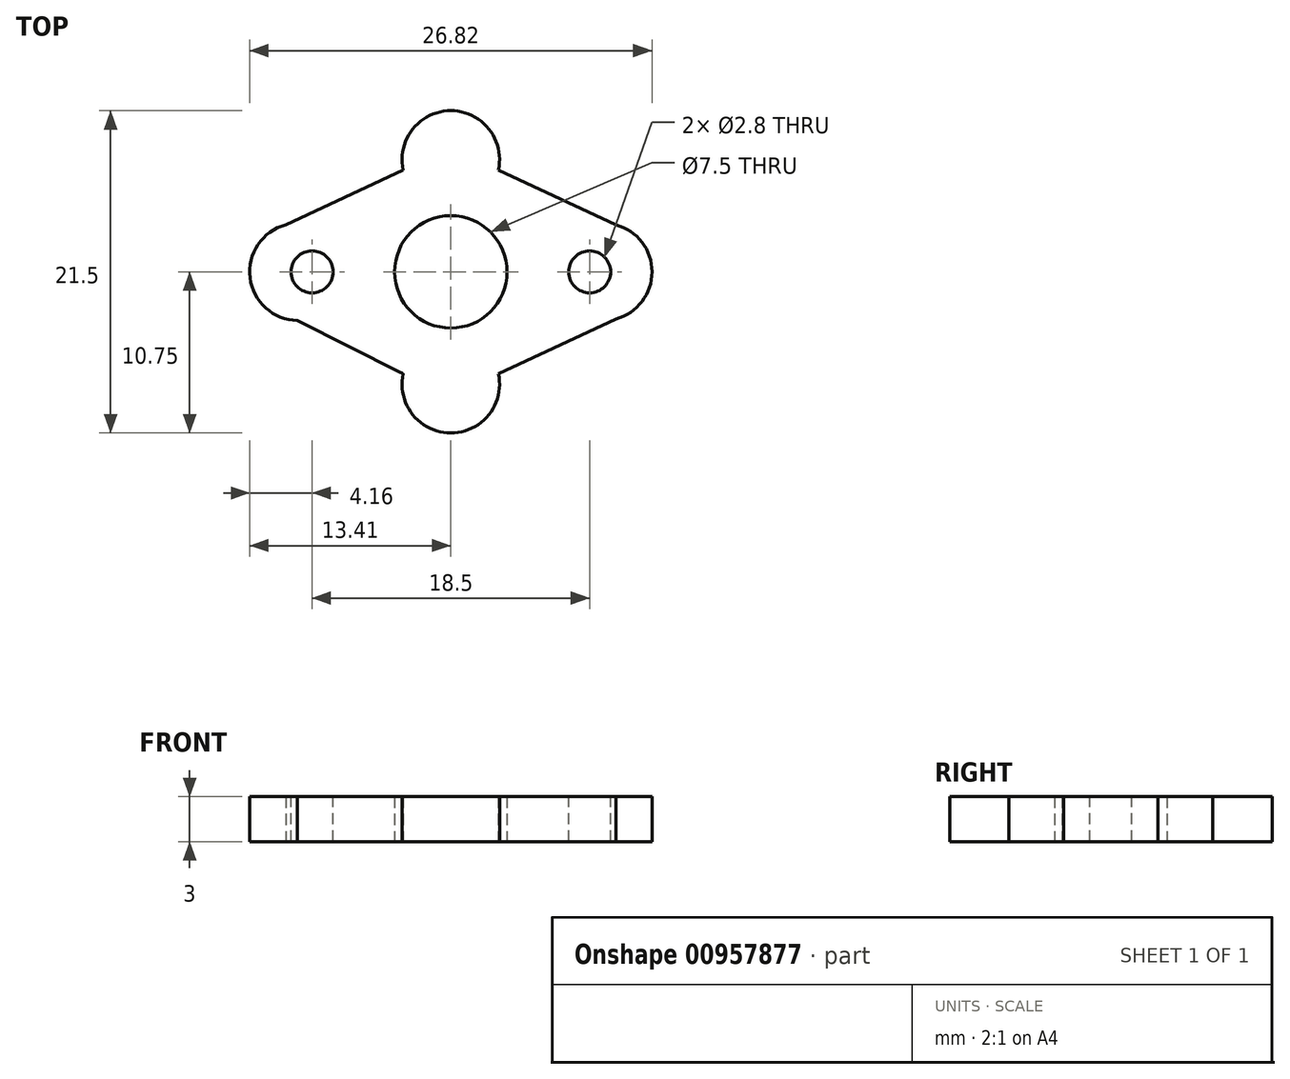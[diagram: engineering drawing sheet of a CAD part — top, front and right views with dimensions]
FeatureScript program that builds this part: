
annotation { "Feature Type Name" : "Feature", "Feature Type Description" : "" }
export const myFeature = defineFeature(function(context is Context, id is Id, definition is map)
    precondition{}
    {
        {
            var Q0;
            Q0=qCreatedBy(makeId("Top.planeOp"),FACE);
            var sketch = newSketch(context, id + "F0", { "sketchPlane" : qUnion([Q0])});
            skCircle(sketch, "E0", {"center": v(0, 0) * mm, "radius": 3.75 * mm});
            skCircle(sketch, "E1", {"center": v(0, 0) * mm, "radius": 7.5 * mm});
            skCircle(sketch, "E2", {"center": v(0, -7.5) * mm, "radius": 3.25 * mm});
            skCircle(sketch, "E3", {"center": v(10.16, 0) * mm, "radius": 3.25 * mm});
            skCircle(sketch, "E4", {"center": v(0, 7.5) * mm, "radius": 3.25 * mm});
            skCircle(sketch, "E5", {"center": v(-10.16, 0) * mm, "radius": 3.25 * mm});
            skLineSegment(sketch, "E6", {"start": v(-10.22, -3.25) * mm, "end": v(-3.17, -6.8) * mm});
            skLineSegment(sketch, "E7", {"start": v(3.17, -6.8) * mm, "end": v(11, -3.14) * mm});
            skLineSegment(sketch, "E8", {"start": v(3.17, 6.8) * mm, "end": v(11, 3.14) * mm});
            skLineSegment(sketch, "E9", {"start": v(-3.17, 6.8) * mm, "end": v(-11, 3.14) * mm});
            skSolve(sketch);
        }
        {
            var Q0;
            {var subQ0=sQuery(id+"F0.wireOp",EDGE,"E4");var subQ1=sQuery(id+"F0.wireOp",EDGE,"E1");var subQ2=makeQuery(id+"F0.imprint","INTERSECT",VERTEX,{"derivedFrom":[subQ1,subQ0,sQuery(id+"F0.wireOp",EDGE,"MsoxRcEN-taFl-h5Oa-m4Po-DjfKg65qIXiD")]});Q0=makeQuery(id+"F0.imprint","IMPRINT",FACE,{"disambiguationData":[TD([[makeQuery(id+"F0.imprint","IMPRINT",EDGE,{"disambiguationData":[TD([[subQ2,-1.0]])],"derivedFrom":subQ1}),-1.0]])]});}
            var Q1;
            {var subQ0=sQuery(id+"F0.wireOp",EDGE,"E5");var subQ1=sQuery(id+"F0.wireOp",EDGE,"E1");var subQ2=makeQuery(id+"F0.imprint","INTERSECT",VERTEX,{"derivedFrom":[subQ1,subQ0,sQuery(id+"F0.wireOp",EDGE,"5fAFj8NA-k12Z-kT6c-h5jL-KaeJKLKDLutY")]});Q1=makeQuery(id+"F0.imprint","IMPRINT",FACE,{"disambiguationData":[TD([[makeQuery(id+"F0.imprint","IMPRINT",EDGE,{"disambiguationData":[TD([[subQ2,1.0]])],"derivedFrom":subQ1}),-1.0]])]});}
            var Q2;
            {var subQ0=sQuery(id+"F0.wireOp",EDGE,"E2");var subQ1=sQuery(id+"F0.wireOp",EDGE,"E1");var subQ2=makeQuery(id+"F0.imprint","INTERSECT",VERTEX,{"derivedFrom":[subQ1,subQ0,sQuery(id+"F0.wireOp",EDGE,"5fAFj8NA-k12Z-kT6c-h5jL-KaeJKLKDLutY")]});Q2=makeQuery(id+"F0.imprint","IMPRINT",FACE,{"disambiguationData":[TD([[makeQuery(id+"F0.imprint","IMPRINT",EDGE,{"disambiguationData":[TD([[subQ2,-1.0]])],"derivedFrom":subQ1}),-1.0]])]});}
            var Q3;
            {var subQ0=sQuery(id+"F0.wireOp",EDGE,"E3");var subQ1=sQuery(id+"F0.wireOp",EDGE,"E1");var subQ2=makeQuery(id+"F0.imprint","INTERSECT",VERTEX,{"derivedFrom":[subQ1,subQ0,sQuery(id+"F0.wireOp",EDGE,"UtXMOaHf-onAp-QZEp-fR57-lMSn8MbB5BsG")]});Q3=makeQuery(id+"F0.imprint","IMPRINT",FACE,{"disambiguationData":[TD([[makeQuery(id+"F0.imprint","IMPRINT",EDGE,{"disambiguationData":[TD([[subQ2,-1.0]])],"derivedFrom":subQ1}),-1.0]])]});}
            var Q4;
            {var subQ0=sQuery(id+"F0.wireOp",EDGE,"UtXMOaHf-onAp-QZEp-fR57-lMSn8MbB5BsG");var subQ1=sQuery(id+"F0.wireOp",EDGE,"E2");var subQ3=makeQuery(id+"F0.imprint","INTERSECT",VERTEX,{"derivedFrom":[subQ1,subQ0]});Q4=makeQuery(id+"F0.imprint","IMPRINT",FACE,{"disambiguationData":[TD([[makeQuery(id+"F0.imprint","IMPRINT",EDGE,{"disambiguationData":[TD([[subQ3,1.0]])],"derivedFrom":subQ1}),1.0]])]});}
            var Q5;
            {var subQ0=sQuery(id+"F0.wireOp",EDGE,"5fAFj8NA-k12Z-kT6c-h5jL-KaeJKLKDLutY");var subQ1=sQuery(id+"F0.wireOp",EDGE,"E2");var subQ3=makeQuery(id+"F0.imprint","INTERSECT",VERTEX,{"derivedFrom":[subQ1,subQ0]});Q5=makeQuery(id+"F0.imprint","IMPRINT",FACE,{"disambiguationData":[TD([[makeQuery(id+"F0.imprint","IMPRINT",EDGE,{"disambiguationData":[TD([[subQ3,-1.0]])],"derivedFrom":subQ1}),1.0]])]});}
            var Q6;
            {var subQ0=sQuery(id+"F0.wireOp",EDGE,"MsoxRcEN-taFl-h5Oa-m4Po-DjfKg65qIXiD");var subQ1=sQuery(id+"F0.wireOp",EDGE,"E3");var subQ3=makeQuery(id+"F0.imprint","INTERSECT",VERTEX,{"derivedFrom":[subQ1,subQ0]});Q6=makeQuery(id+"F0.imprint","IMPRINT",FACE,{"disambiguationData":[TD([[makeQuery(id+"F0.imprint","IMPRINT",EDGE,{"disambiguationData":[TD([[subQ3,1.0]])],"derivedFrom":subQ1}),1.0]])]});}
            var Q7;
            {var subQ0=sQuery(id+"F0.wireOp",EDGE,"UtXMOaHf-onAp-QZEp-fR57-lMSn8MbB5BsG");var subQ1=sQuery(id+"F0.wireOp",EDGE,"E3");var subQ3=makeQuery(id+"F0.imprint","INTERSECT",VERTEX,{"derivedFrom":[subQ1,subQ0]});Q7=makeQuery(id+"F0.imprint","IMPRINT",FACE,{"disambiguationData":[TD([[makeQuery(id+"F0.imprint","IMPRINT",EDGE,{"disambiguationData":[TD([[subQ3,-1.0]])],"derivedFrom":subQ1}),1.0]])]});}
            var Q8;
            {var subQ0=sQuery(id+"F0.wireOp",EDGE,"tvJ5aQMQ-Ffmk-I155-r6WP-GNYaoDp2G4Gd");var subQ1=sQuery(id+"F0.wireOp",EDGE,"E4");var subQ3=makeQuery(id+"F0.imprint","INTERSECT",VERTEX,{"derivedFrom":[subQ1,subQ0]});Q8=makeQuery(id+"F0.imprint","IMPRINT",FACE,{"disambiguationData":[TD([[makeQuery(id+"F0.imprint","IMPRINT",EDGE,{"disambiguationData":[TD([[subQ3,1.0]])],"derivedFrom":subQ1}),1.0]])]});}
            var Q9;
            {var subQ0=sQuery(id+"F0.wireOp",EDGE,"MsoxRcEN-taFl-h5Oa-m4Po-DjfKg65qIXiD");var subQ1=sQuery(id+"F0.wireOp",EDGE,"E4");var subQ3=makeQuery(id+"F0.imprint","INTERSECT",VERTEX,{"derivedFrom":[subQ1,subQ0]});Q9=makeQuery(id+"F0.imprint","IMPRINT",FACE,{"disambiguationData":[TD([[makeQuery(id+"F0.imprint","IMPRINT",EDGE,{"disambiguationData":[TD([[subQ3,-1.0]])],"derivedFrom":subQ1}),1.0]])]});}
            var Q10;
            {var subQ0=sQuery(id+"F0.wireOp",EDGE,"tvJ5aQMQ-Ffmk-I155-r6WP-GNYaoDp2G4Gd");var subQ1=sQuery(id+"F0.wireOp",EDGE,"E5");var subQ3=makeQuery(id+"F0.imprint","INTERSECT",VERTEX,{"derivedFrom":[subQ1,subQ0]});Q10=makeQuery(id+"F0.imprint","IMPRINT",FACE,{"disambiguationData":[TD([[makeQuery(id+"F0.imprint","IMPRINT",EDGE,{"disambiguationData":[TD([[subQ3,-1.0]])],"derivedFrom":subQ1}),1.0]])]});}
            var Q11;
            {var subQ0=sQuery(id+"F0.wireOp",EDGE,"5fAFj8NA-k12Z-kT6c-h5jL-KaeJKLKDLutY");var subQ1=sQuery(id+"F0.wireOp",EDGE,"E5");var subQ3=makeQuery(id+"F0.imprint","INTERSECT",VERTEX,{"derivedFrom":[subQ1,subQ0]});Q11=makeQuery(id+"F0.imprint","IMPRINT",FACE,{"disambiguationData":[TD([[makeQuery(id+"F0.imprint","IMPRINT",EDGE,{"disambiguationData":[TD([[subQ3,1.0]])],"derivedFrom":subQ1}),1.0]])]});}
            var Q12;
            {var subQ1=sQuery(id+"F0.wireOp",EDGE,"E4");var subQ4=sQuery(id+"F0.wireOp",EDGE,"tvJ5aQMQ-Ffmk-I155-r6WP-GNYaoDp2G4Gd");var subQ6=makeQuery(id+"F0.imprint","INTERSECT",VERTEX,{"derivedFrom":[subQ1,subQ4]});Q12=makeQuery(id+"F0.imprint","IMPRINT",FACE,{"disambiguationData":[TD([[makeQuery(id+"F0.imprint","IMPRINT",EDGE,{"disambiguationData":[TD([[subQ6,-1.0]])],"derivedFrom":subQ1}),1.0]])]});}
            var Q13;
            {var subQ1=sQuery(id+"F0.wireOp",EDGE,"E5");var subQ4=sQuery(id+"F0.wireOp",EDGE,"tvJ5aQMQ-Ffmk-I155-r6WP-GNYaoDp2G4Gd");var subQ6=makeQuery(id+"F0.imprint","INTERSECT",VERTEX,{"derivedFrom":[subQ1,subQ4]});Q13=makeQuery(id+"F0.imprint","IMPRINT",FACE,{"disambiguationData":[TD([[makeQuery(id+"F0.imprint","IMPRINT",EDGE,{"disambiguationData":[TD([[subQ6,1.0]])],"derivedFrom":subQ1}),1.0]])]});}
            var Q14;
            {var subQ1=sQuery(id+"F0.wireOp",EDGE,"E2");var subQ4=sQuery(id+"F0.wireOp",EDGE,"UtXMOaHf-onAp-QZEp-fR57-lMSn8MbB5BsG");var subQ6=makeQuery(id+"F0.imprint","INTERSECT",VERTEX,{"derivedFrom":[subQ1,subQ4]});Q14=makeQuery(id+"F0.imprint","IMPRINT",FACE,{"disambiguationData":[TD([[makeQuery(id+"F0.imprint","IMPRINT",EDGE,{"disambiguationData":[TD([[subQ6,-1.0]])],"derivedFrom":subQ1}),1.0]])]});}
            var Q15;
            {var subQ1=sQuery(id+"F0.wireOp",EDGE,"E3");var subQ4=sQuery(id+"F0.wireOp",EDGE,"MsoxRcEN-taFl-h5Oa-m4Po-DjfKg65qIXiD");var subQ7=makeQuery(id+"F0.imprint","INTERSECT",VERTEX,{"derivedFrom":[subQ1,subQ4]});Q15=makeQuery(id+"F0.imprint","IMPRINT",FACE,{"disambiguationData":[TD([[makeQuery(id+"F0.imprint","IMPRINT",EDGE,{"disambiguationData":[TD([[subQ7,-1.0]])],"derivedFrom":subQ1}),1.0]])]});}
            var Q16;
            {var subQ0=sQuery(id+"F0.wireOp",EDGE,"E6");var subQ1=sQuery(id+"F0.wireOp",EDGE,"E1");var subQ2=makeQuery(id+"F0.imprint","INTERSECT",VERTEX,{"derivedFrom":[subQ1,subQ0]});Q16=makeQuery(id+"F0.imprint","IMPRINT",FACE,{"disambiguationData":[TD([[makeQuery(id+"F0.imprint","IMPRINT",EDGE,{"disambiguationData":[TD([[subQ2,1.0]])],"derivedFrom":subQ1}),-1.0]])]});}
            var Q17;
            {var subQ0=sQuery(id+"F0.wireOp",EDGE,"E7");Q17=makeQuery(id+"F0.imprint","IMPRINT",FACE,{"disambiguationData":[TD([[makeQuery(id+"F0.imprint","IMPRINT",EDGE,{"derivedFrom":subQ0}),1.0]])]});}
            var Q18;
            {var subQ0=sQuery(id+"F0.wireOp",EDGE,"E3");var subQ1=sQuery(id+"F0.wireOp",EDGE,"E1");var subQ2=makeQuery(id+"F0.imprint","INTERSECT",VERTEX,{"disambiguationData":[OD(0.0)],"derivedFrom":[subQ1,subQ0]});Q18=makeQuery(id+"F0.imprint","IMPRINT",FACE,{"disambiguationData":[TD([[makeQuery(id+"F0.imprint","IMPRINT",EDGE,{"disambiguationData":[TD([[subQ2,1.0]])],"derivedFrom":subQ1}),1.0]])]});}
            var Q19;
            Q19=makeQuery(id+"F0.imprint","IMPRINT",FACE,{"disambiguationData":[TD([[makeQuery(id+"F0.imprint","IMPRINT",EDGE,{"derivedFrom":sQuery(id+"F0.wireOp",EDGE,"E0")}),-1.0]])]});
            var Q20;
            {var subQ0=sQuery(id+"F0.wireOp",EDGE,"E5");var subQ1=sQuery(id+"F0.wireOp",EDGE,"E1");var subQ2=makeQuery(id+"F0.imprint","INTERSECT",VERTEX,{"disambiguationData":[OD(0.0)],"derivedFrom":[subQ1,subQ0]});Q20=makeQuery(id+"F0.imprint","IMPRINT",FACE,{"disambiguationData":[TD([[makeQuery(id+"F0.imprint","IMPRINT",EDGE,{"disambiguationData":[TD([[subQ2,-1.0]])],"derivedFrom":subQ1}),1.0]])]});}
            extrude(context, id + "F1", {"entities" : qUnion([Q0, Q1, Q2, Q3, Q4, Q5, Q6, Q7, Q8, Q9, Q10, Q11, Q12, Q13, Q14, Q15, Q16, Q17, Q18, Q19, Q20]), "depth" : 3 * mm, "offsetDistance" : 25.4 * mm});
        }
        {
            var Q0;
            Q0=makeQuery(id+"F1.opExtrude","CAP_FACE",FACE,{"disambiguationData":[OSD([sQuery(id+"F0.wireOp",EDGE,"E0"),sQuery(id+"F0.wireOp",EDGE,"E2"),sQuery(id+"F0.wireOp",EDGE,"E3"),sQuery(id+"F0.wireOp",EDGE,"E4"),sQuery(id+"F0.wireOp",EDGE,"E5"),sQuery(id+"F0.wireOp",EDGE,"5fAFj8NA-k12Z-kT6c-h5jL-KaeJKLKDLutY"),sQuery(id+"F0.wireOp",EDGE,"UtXMOaHf-onAp-QZEp-fR57-lMSn8MbB5BsG"),sQuery(id+"F0.wireOp",EDGE,"MsoxRcEN-taFl-h5Oa-m4Po-DjfKg65qIXiD"),sQuery(id+"F0.wireOp",EDGE,"tvJ5aQMQ-Ffmk-I155-r6WP-GNYaoDp2G4Gd")])],"isStart":false});
            var sketch = newSketch(context, id + "F2", { "sketchPlane" : qUnion([Q0])});
            skCircle(sketch, "E10", {"center": v(-9.25, 0) * mm, "radius": 1.4 * mm});
            skCircle(sketch, "E11", {"center": v(9.25, 0) * mm, "radius": 1.4 * mm});
            skSolve(sketch);
        }
        {
            var Q0;
            Q0=makeQuery(id+"F2.imprint","IMPRINT",FACE,{"disambiguationData":[TD([[makeQuery(id+"F2.imprint","IMPRINT",EDGE,{"derivedFrom":sQuery(id+"F2.wireOp",EDGE,"E10")}),1.0]])]});
            var Q1;
            Q1=makeQuery(id+"F2.imprint","IMPRINT",FACE,{"disambiguationData":[TD([[makeQuery(id+"F2.imprint","IMPRINT",EDGE,{"derivedFrom":sQuery(id+"F2.wireOp",EDGE,"E11")}),1.0]])]});
            extrude(context, id + "F3", {"entities" : qUnion([Q0, Q1]), "operationType" : NewBodyOperationType.REMOVE, "oppositeDirection" : true, "depth" : 6.1 * mm, "offsetDistance" : 25.4 * mm});
        }
    });
